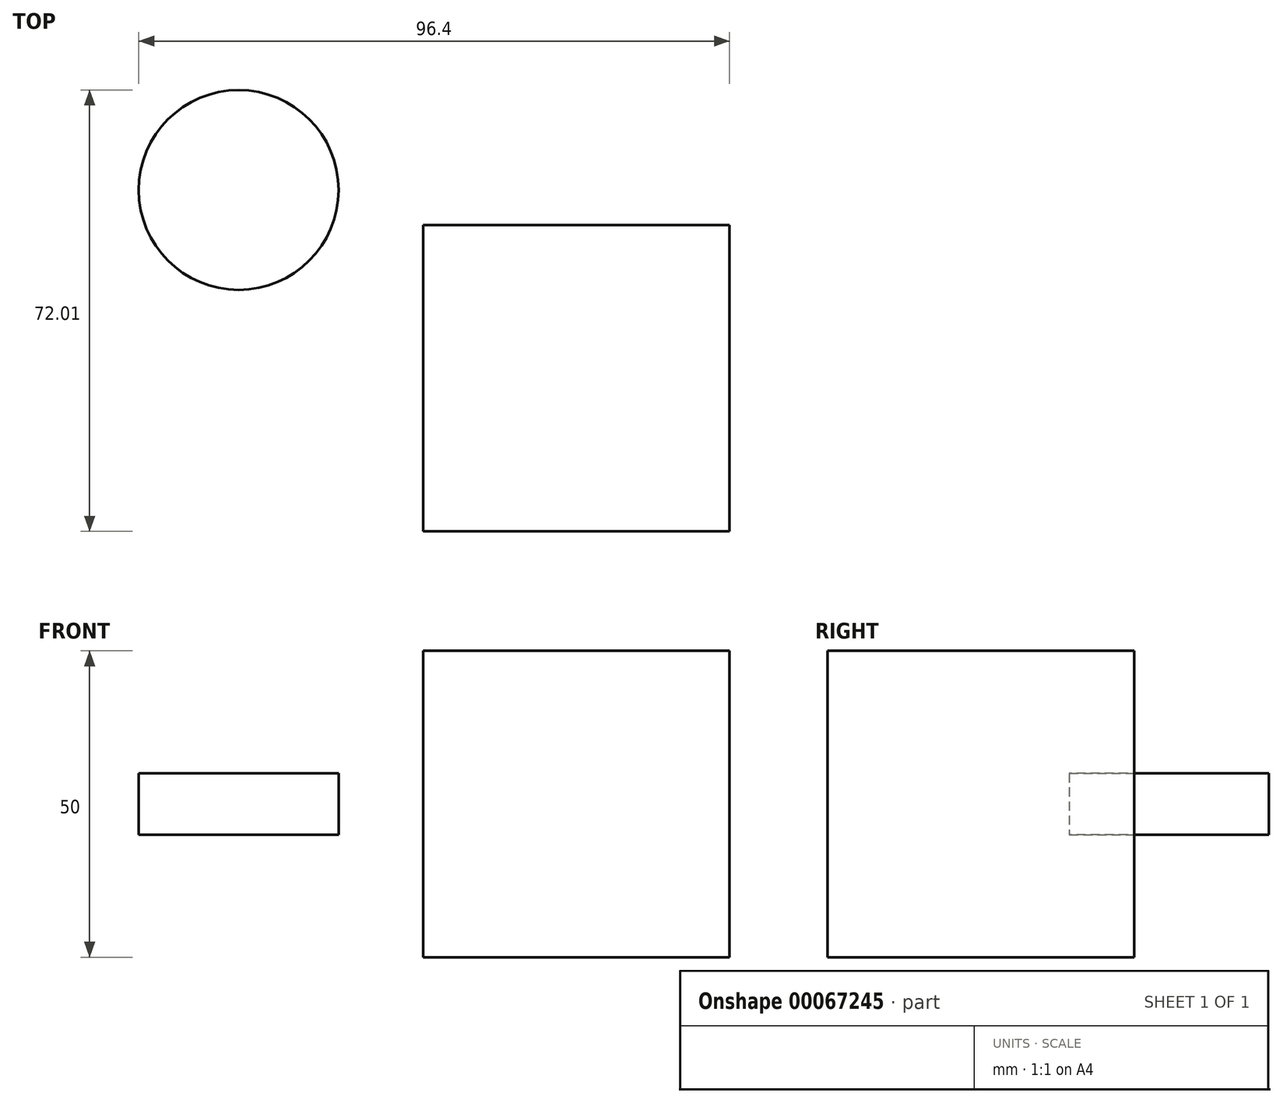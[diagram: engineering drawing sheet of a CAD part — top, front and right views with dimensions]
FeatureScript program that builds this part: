
annotation { "Feature Type Name" : "Feature", "Feature Type Description" : "" }
export const myFeature = defineFeature(function(context is Context, id is Id, definition is map)
    precondition{}
    {
        {
            var Q0;
            Q0=qCreatedBy(makeId("Top.planeOp"),FACE);
            var sketch = newSketch(context, id + "F0", { "sketchPlane" : qUnion([Q0])});
            skLineSegment(sketch, "E0.rect.bottom", {"start": v(25, -25) * mm, "end": v(-25, -25) * mm});
            skLineSegment(sketch, "E0.rect.top", {"start": v(25, 25) * mm, "end": v(-25, 25) * mm});
            skLineSegment(sketch, "E0.rect.left", {"start": v(25, -25) * mm, "end": v(25, 25) * mm});
            skLineSegment(sketch, "E0.rect.right", {"start": v(-25, -25) * mm, "end": v(-25, 25) * mm});
            skPoint(sketch, "E0.rect.middle", {"position": v(0, 0) * mm});
            skSolve(sketch);
        }
        {
            var Q0;
            Q0 = qSketchRegion(id + "F0", true);
            extrude(context, id + "F1", {"entities" : qUnion([Q0]), "endBound" : BoundingType.SYMMETRIC, "depth" : 50 * mm});
        }
        {
            var Q0;
            Q0=qCreatedBy(makeId("Top.planeOp"),FACE);
            var sketch = newSketch(context, id + "F2", { "sketchPlane" : qUnion([Q0])});
            skCircle(sketch, "E1", {"center": v(-55.1, 30.7) * mm, "radius": 16.3 * mm});
            skSolve(sketch);
        }
        {
            var Q0;
            Q0 = qSketchRegion(id + "F2", true);
            extrude(context, id + "F3", {"entities" : qUnion([Q0]), "endBound" : BoundingType.SYMMETRIC, "depth" : 10 * mm});
        }
    });
